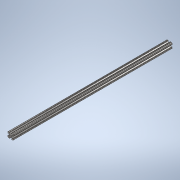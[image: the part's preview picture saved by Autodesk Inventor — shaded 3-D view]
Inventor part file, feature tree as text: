
AUTODESK INVENTOR PART (.ipt)
format: ipt  version: 2020 (Build 240168000, 168)  size: 244,224 bytes
history: native  units: in
note: dims shown in document units (in); Inventor stores cm internally (conversion verified against a paired STEP export)
features: extrude x1, sketch x1
ambient origin geometry x8: Origin, YZ Plane, XZ Plane, XY Plane, X Axis, Y Axis, Z Axis, Center Point
bodies: Solid1 (feature_tree)
feature tree (2):
  extrude  "Extrusion1"  [1 undecoded]
  sketch  "Sketch1"  dims[d0=29.0in d1=0.0in]
note: 1 required parameter value undecoded (feature->parameter linkage not recoverable at this tier; creation-order binding heuristic only, values carry confidence <= 0.55)
